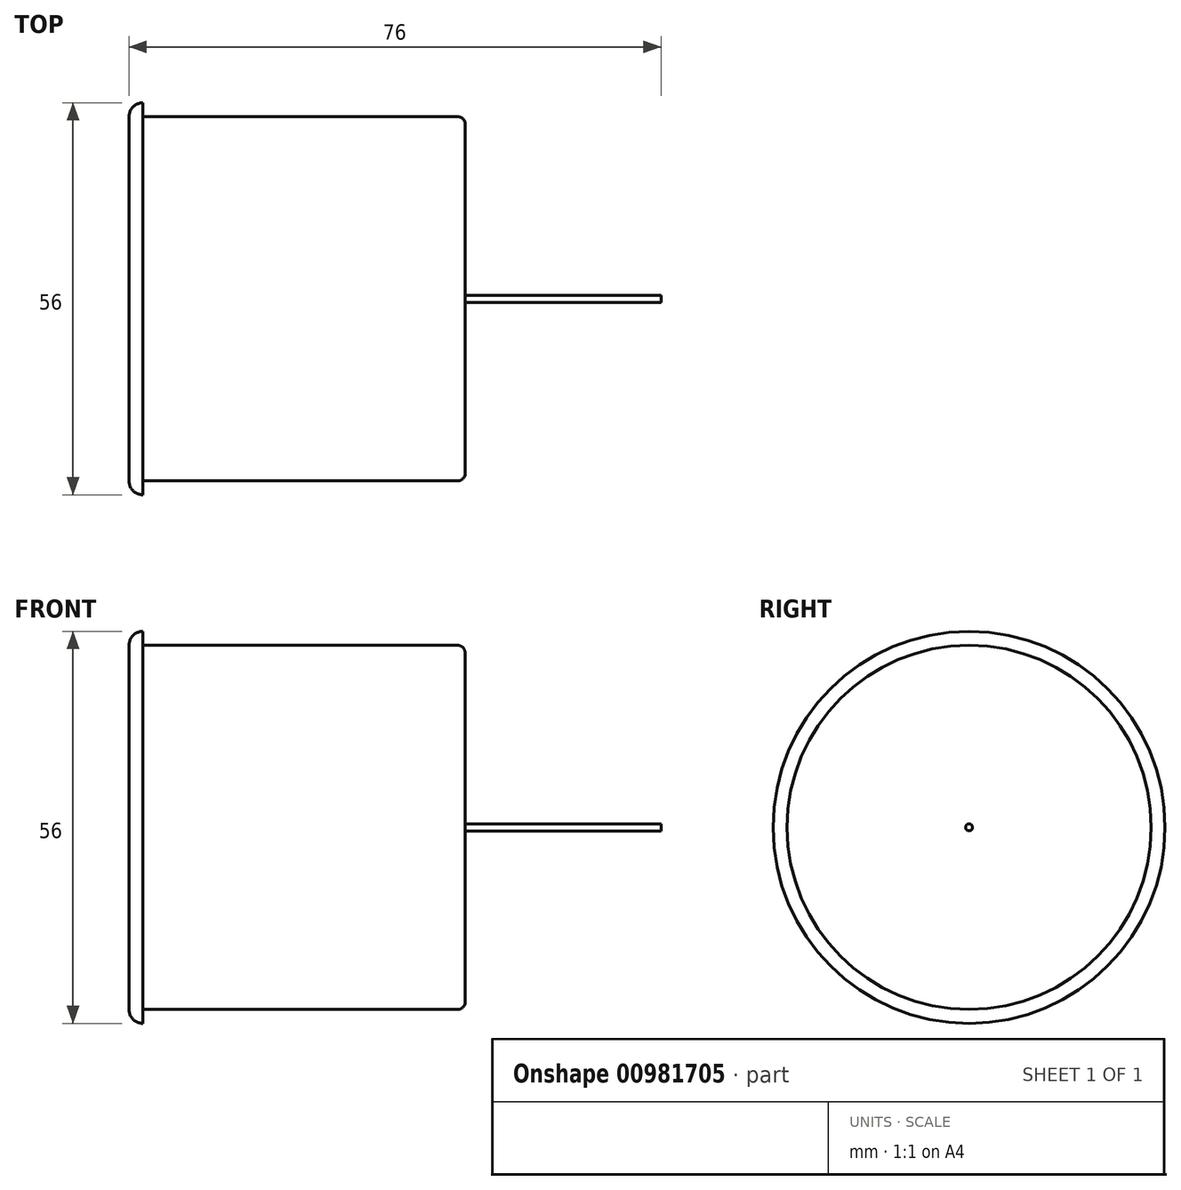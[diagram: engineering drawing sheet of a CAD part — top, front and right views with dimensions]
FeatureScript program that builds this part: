
annotation { "Feature Type Name" : "Feature", "Feature Type Description" : "" }
export const myFeature = defineFeature(function(context is Context, id is Id, definition is map)
    precondition{}
    {
        {
            var Q0;
            Q0=qCreatedBy(makeId("Front.planeOp"),FACE);
            var sketch = newSketch(context, id + "F0", { "sketchPlane" : qUnion([Q0])});
            skLineSegment(sketch, "E0", {"start": v(-99.2, 0) * mm, "end": v(46.93, 0) * mm, "construction": true});
            skLineSegment(sketch, "E1", {"start": v(-0.07, 26) * mm, "end": v(-0.07, 0) * mm});
            skArc(sketch, "E2", {"start": v(-0.07, 26) * mm, "mid": v(0.52, 27.41) * mm, "end": v(1.93, 28) * mm});
            skLineSegment(sketch, "E3", {"start": v(1.93, 28) * mm, "end": v(1.93, 0) * mm});
            skLineSegment(sketch, "E4", {"start": v(1.93, 0) * mm, "end": v(-0.07, 0) * mm});
            skLineSegment(sketch, "E5.bottom", {"start": v(1.93, 26) * mm, "end": v(46.93, 26) * mm});
            skLineSegment(sketch, "E5.top", {"start": v(1.93, 0) * mm, "end": v(47.93, 0) * mm});
            skLineSegment(sketch, "E5.left", {"start": v(1.93, 26) * mm, "end": v(1.93, 0) * mm});
            skLineSegment(sketch, "E5.right", {"start": v(47.93, 25) * mm, "end": v(47.93, 1) * mm});
            skPoint(sketch, "E6.visualSharp", {"position": v(47.93, 26) * mm});
            skArc(sketch, "E6.filletArc", {"start": v(47.93, 25) * mm, "mid": v(47.64, 25.7) * mm, "end": v(46.93, 26) * mm});
            skArc(sketch, "E7.filletArc", {"start": v(46.93, 0) * mm, "mid": v(47.64, 0.3) * mm, "end": v(47.93, 1) * mm});
            skSolve(sketch);
        }
        {
            var Q0;
            Q0 = qSketchRegion(id + "F0", true);
            var Q1;
            Q1=sQuery(id+"F0.wireOp",EDGE,"E0");
            revolve(context, id + "F1", {"surfaceOperationType" : NewSurfaceOperationType.NEW, "entities" : qUnion([Q0]), "axis" : qUnion([Q1]), "revolveType" : RevolveType.FULL});
        }
        {
            var Q0;
            Q0=qCreatedBy(makeId("Right.planeOp"),FACE);
            var sketch = newSketch(context, id + "F2", { "sketchPlane" : qUnion([Q0])});
            skCircle(sketch, "E8", {"center": v(0, 0) * mm, "radius": 1 * mm});
            skSolve(sketch);
        }
        {
            var Q0;
            Q0 = qSketchRegion(id + "F2", true);
            extrude(context, id + "F3", {"entities" : qUnion([Q0]), "operationType" : NewBodyOperationType.ADD, "depth" : (73 - 45) * mm, "offsetDistance" : 25 * mm});
        }
        {
            var Q0;
            Q0=qCreatedBy(makeId("Front.planeOp"),FACE);
            var sketch = newSketch(context, id + "F4", { "sketchPlane" : qUnion([Q0])});
            skLineSegment(sketch, "E9.bottom", {"start": v(47.93, 0) * mm, "end": v(75.93, 0) * mm});
            skLineSegment(sketch, "E9.top", {"start": v(47.93, 0.5) * mm, "end": v(75.93, 0.5) * mm});
            skLineSegment(sketch, "E9.left", {"start": v(47.93, 0) * mm, "end": v(47.93, 0.5) * mm});
            skLineSegment(sketch, "E9.right", {"start": v(75.93, 0) * mm, "end": v(75.93, 0.5) * mm});
            skSolve(sketch);
        }
        {
            var Q0;
            Q0 = qSketchRegion(id + "F4", true);
            var Q1;
            Q1=sQuery(id+"F0.wireOp",EDGE,"E0");
            revolve(context, id + "F5", {"operationType" : NewBodyOperationType.ADD, "surfaceOperationType" : NewSurfaceOperationType.NEW, "entities" : qUnion([Q0]), "axis" : qUnion([Q1]), "revolveType" : RevolveType.FULL});
        }
    });
